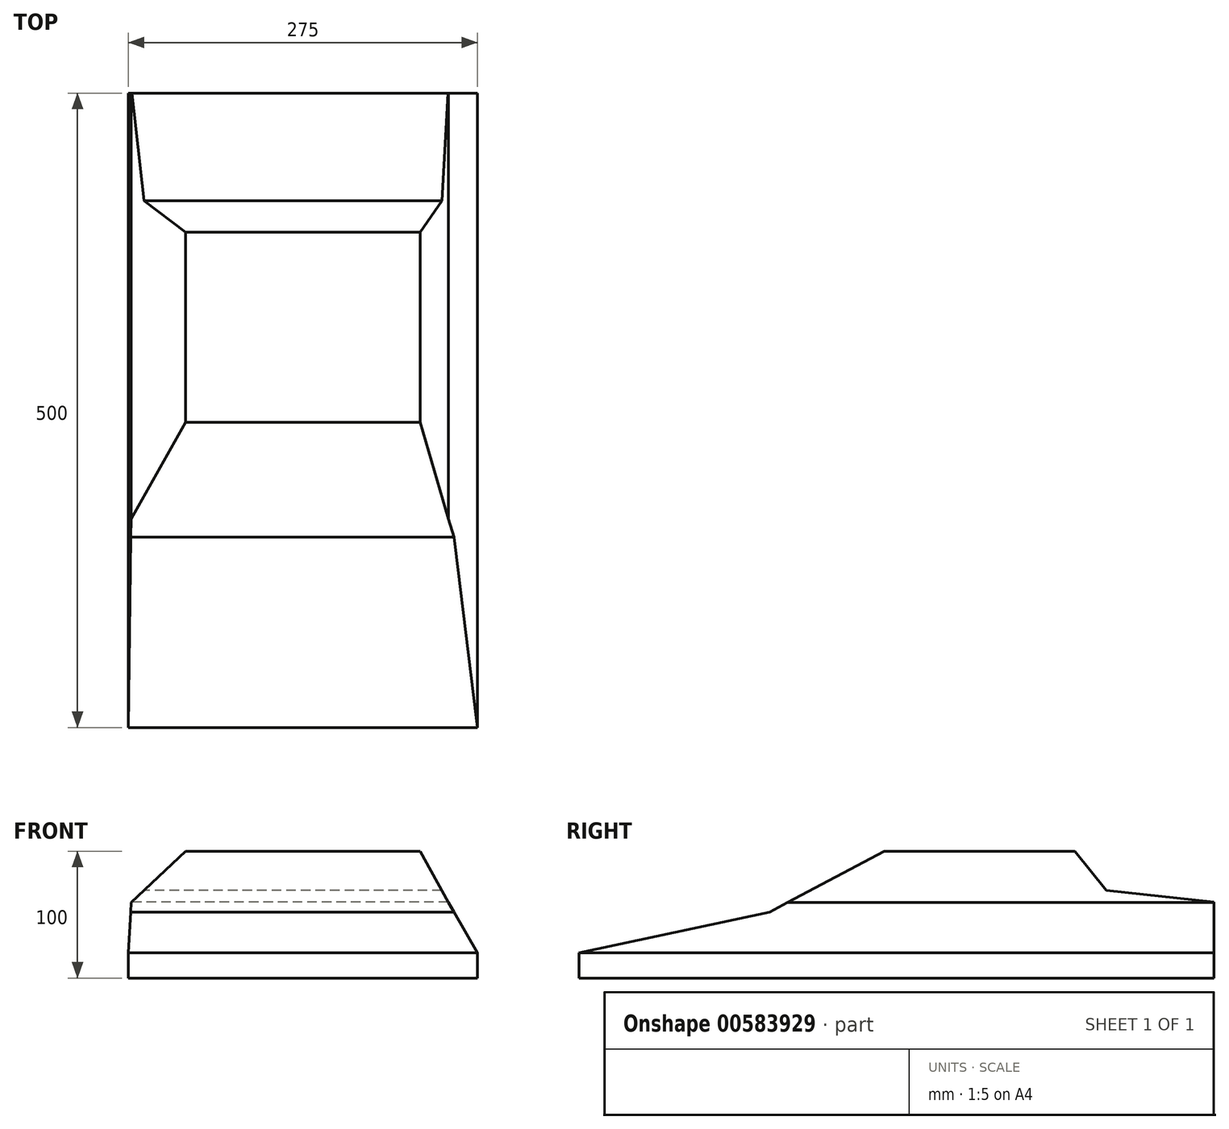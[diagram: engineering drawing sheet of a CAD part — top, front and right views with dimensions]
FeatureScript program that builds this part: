
annotation { "Feature Type Name" : "Feature", "Feature Type Description" : "" }
export const myFeature = defineFeature(function(context is Context, id is Id, definition is map)
    precondition{}
    {
        {
            var Q0;
            Q0=qCreatedBy(makeId("Right.planeOp"),FACE);
            var sketch = newSketch(context, id + "F0", { "sketchPlane" : qUnion([Q0])});
            skLineSegment(sketch, "E0", {"start": v(-150, 0) * mm, "end": v(-150, 20) * mm});
            skLineSegment(sketch, "E1", {"start": v(-150, 20) * mm, "end": v(0, 51.88) * mm});
            skLineSegment(sketch, "E2", {"start": v(350, 60) * mm, "end": v(350, 0) * mm});
            skLineSegment(sketch, "E3", {"start": v(350, 0) * mm, "end": v(-150, 0) * mm});
            skLineSegment(sketch, "E4", {"start": v(0, 51.88) * mm, "end": v(90.5, 100) * mm});
            skLineSegment(sketch, "E5", {"start": v(90.5, 100) * mm, "end": v(240.5, 100) * mm});
            skLineSegment(sketch, "E6", {"start": v(240.5, 100) * mm, "end": v(265.21, 69.1) * mm});
            skLineSegment(sketch, "E7", {"start": v(265.21, 69.1) * mm, "end": v(350, 60) * mm});
            skSolve(sketch);
        }
        {
            var Q0;
            Q0=makeQuery(id+"F0.imprint","IMPRINT",FACE,{"disambiguationData":[TD([[makeQuery(id+"F0.imprint","IMPRINT",EDGE,{"derivedFrom":sQuery(id+"F0.wireOp",EDGE,"E0")}),-1.0]])]});
            extrude(context, id + "F1", {"entities" : qUnion([Q0]), "depth" : 150 * mm, "hasSecondDirection" : true, "secondDirectionOppositeDirection" : true, "secondDirectionDepth" : 125 * mm});
        }
        {
            var Q0;
            Q0=makeQuery(id+"F1.opExtrude","SWEPT_FACE",FACE,{"disambiguationData":[OSD([sQuery(id+"F0.wireOp",EDGE,"E2")])]});
            var sketch = newSketch(context, id + "F2", { "sketchPlane" : qUnion([Q0])});
            skLineSegment(sketch, "E8", {"start": v(80, 100) * mm, "end": v(-105, 100) * mm});
            skLineSegment(sketch, "E9", {"start": v(-105, 100) * mm, "end": v(-127.24, 59.43) * mm});
            skLineSegment(sketch, "E10", {"start": v(125, 20) * mm, "end": v(125, 0) * mm});
            skLineSegment(sketch, "E11", {"start": v(125, 0) * mm, "end": v(-150, 0) * mm});
            skLineSegment(sketch, "E12", {"start": v(-150, 0) * mm, "end": v(-150, 20) * mm});
            skLineSegment(sketch, "E13", {"start": v(80, 100) * mm, "end": v(125, 100) * mm, "construction": true});
            skLineSegment(sketch, "E14", {"start": v(-105, 100) * mm, "end": v(-150, 100) * mm, "construction": true});
            skLineSegment(sketch, "E15", {"start": v(122.76, 59.43) * mm, "end": v(80, 100) * mm});
            skLineSegment(sketch, "E16", {"start": v(-131.7, 51.28) * mm, "end": v(-131.7, 51.28) * mm});
            skLineSegment(sketch, "E17", {"start": v(122.76, 59.43) * mm, "end": v(-127.24, 59.43) * mm, "construction": true});
            skLineSegment(sketch, "E18", {"start": v(122.76, 59.43) * mm, "end": v(125, 20) * mm});
            skLineSegment(sketch, "E19", {"start": v(-127.24, 59.43) * mm, "end": v(-150, 20) * mm});
            skSolve(sketch);
        }
        {
            var Q0;
            Q0=qSketchRegion(id+"F2",true);
            extrude(context, id + "F3", {"entities" : qUnion([Q0]), "operationType" : NewBodyOperationType.INTERSECT, "oppositeDirection" : true, "depth" : 2000 * mm});
        }
    });
